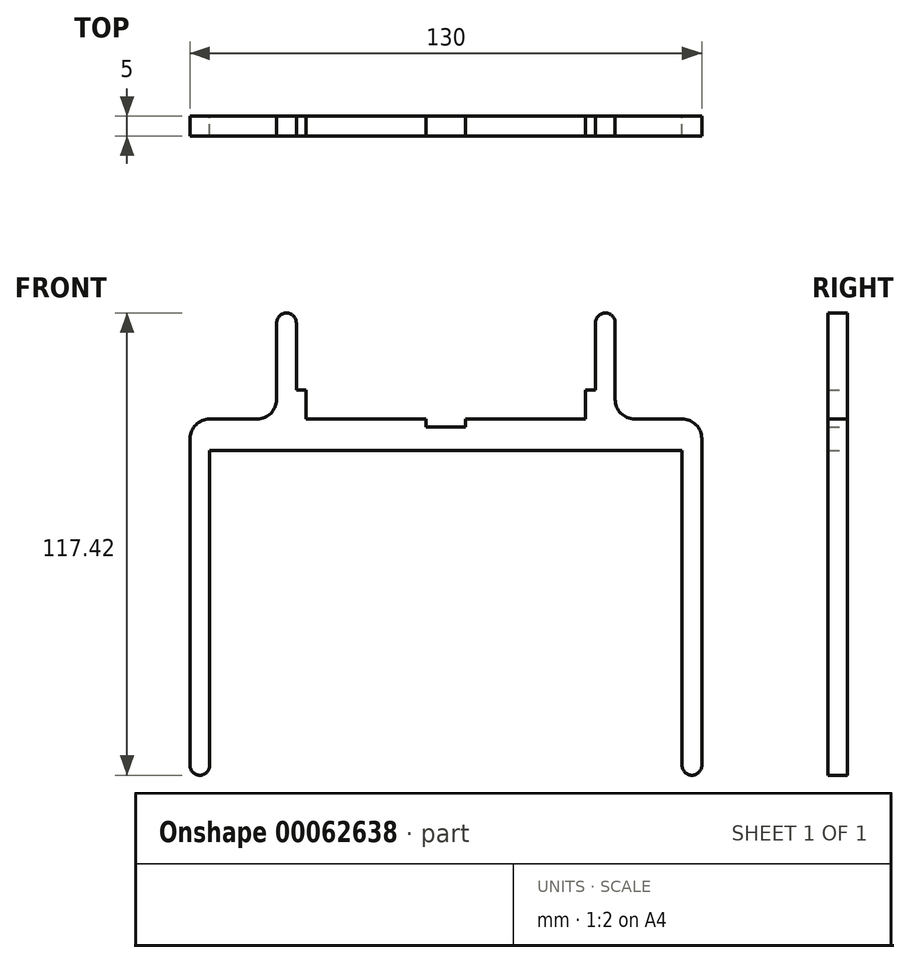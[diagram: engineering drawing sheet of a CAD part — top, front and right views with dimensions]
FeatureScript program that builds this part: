
annotation { "Feature Type Name" : "Feature", "Feature Type Description" : "" }
export const myFeature = defineFeature(function(context is Context, id is Id, definition is map)
    precondition{}
    {
        {
            var Q0;
            Q0=qCreatedBy(makeId("Front.planeOp"),FACE);
            var sketch = newSketch(context, id + "F0", { "sketchPlane" : qUnion([Q0])});
            skLineSegment(sketch, "E0.bottom", {"start": v(-60, 0) * mm, "end": v(0, 0) * mm});
            skLineSegment(sketch, "E0.top", {"start": v(-60, 8) * mm, "end": v(-43, 8) * mm});
            skLineSegment(sketch, "E1.bottom", {"start": v(-60, 8) * mm, "end": v(-65, 8) * mm});
            skLineSegment(sketch, "E1.left", {"start": v(-60, 0) * mm, "end": v(-60, -80) * mm});
            skLineSegment(sketch, "E1.right", {"start": v(-65, 8) * mm, "end": v(-65, -80) * mm});
            skPoint(sketch, "E2", {"position": v(-35.5, 8) * mm});
            skLineSegment(sketch, "E3.top", {"start": v(-35.5, 15.42) * mm, "end": v(-38, 15.42) * mm});
            skLineSegment(sketch, "E3.left", {"start": v(-35.5, 8) * mm, "end": v(-35.5, 15.42) * mm});
            skLineSegment(sketch, "E4.left", {"start": v(-38, 15.42) * mm, "end": v(-38, 32.42) * mm});
            skLineSegment(sketch, "E4.right", {"start": v(-43, 8) * mm, "end": v(-43, 32.42) * mm});
            skLineSegment(sketch, "E5.trimOffspring", {"start": v(-35.5, 8) * mm, "end": v(0, 8) * mm});
            skArc(sketch, "E6", {"start": v(-38, 32.42) * mm, "mid": v(-40.5, 34.92) * mm, "end": v(-43, 32.42) * mm});
            skArc(sketch, "E7", {"start": v(-65, -80) * mm, "mid": v(-62.5, -82.5) * mm, "end": v(-60, -80) * mm});
            skArc(sketch, "E8.MirrorCS", {"start": v(38, 32.42) * mm, "mid": v(40.5, 34.92) * mm, "end": v(43, 32.42) * mm});
            skLineSegment(sketch, "E9.MirrorCS", {"start": v(35.5, 15.42) * mm, "end": v(38, 15.42) * mm});
            skLineSegment(sketch, "E10.MirrorCS", {"start": v(60, 8) * mm, "end": v(65, 8) * mm});
            skLineSegment(sketch, "E11.MirrorCS", {"start": v(60, 8) * mm, "end": v(43, 8) * mm});
            skLineSegment(sketch, "E12.MirrorCS", {"start": v(35.5, 8) * mm, "end": v(35.5, 15.42) * mm});
            skLineSegment(sketch, "E13.MirrorCS", {"start": v(65, 8) * mm, "end": v(65, -80) * mm});
            skPoint(sketch, "E14.MirrorP", {"position": v(35.5, 8) * mm});
            skLineSegment(sketch, "E15.MirrorCS", {"start": v(60, 0) * mm, "end": v(60, -80) * mm});
            skLineSegment(sketch, "E16.MirrorCS", {"start": v(43, 8) * mm, "end": v(43, 32.42) * mm});
            skArc(sketch, "E17.MirrorCS", {"start": v(65, -80) * mm, "mid": v(62.5, -82.5) * mm, "end": v(60, -80) * mm});
            skLineSegment(sketch, "E18.MirrorCS", {"start": v(38, 15.42) * mm, "end": v(38, 32.42) * mm});
            skLineSegment(sketch, "E19.MirrorCS", {"start": v(35.5, 8) * mm, "end": v(0, 8) * mm});
            skLineSegment(sketch, "E20.MirrorCS", {"start": v(60, 0) * mm, "end": v(0, 0) * mm});
            skSolve(sketch);
        }
        {
            var Q0;
            Q0 = qSketchRegion(id + "F0", true);
            extrude(context, id + "F1", {"entities" : qUnion([Q0]), "depth" : 5 * mm});
        }
        {
            var Q0;
            Q0=qCreatedBy(makeId("Front.planeOp"),FACE);
            var sketch = newSketch(context, id + "F2", { "sketchPlane" : qUnion([Q0])});
            skLineSegment(sketch, "E21.rect.bottom", {"start": v(5, 6) * mm, "end": v(-5, 6) * mm});
            skLineSegment(sketch, "E21.rect.top", {"start": v(5, 10) * mm, "end": v(-5, 10) * mm});
            skLineSegment(sketch, "E21.rect.left", {"start": v(5, 6) * mm, "end": v(5, 10) * mm});
            skLineSegment(sketch, "E21.rect.right", {"start": v(-5, 6) * mm, "end": v(-5, 10) * mm});
            skPoint(sketch, "E21.rect.middle", {"position": v(0, 8) * mm});
            skSolve(sketch);
        }
        {
            var Q0;
            Q0 = qSketchRegion(id + "F2", true);
            extrude(context, id + "F3", {"entities" : qUnion([Q0]), "operationType" : NewBodyOperationType.REMOVE, "depth" : 25 * mm});
        }
        {
            var Q0;
            Q0=makeQuery(id+"F1.opExtrude","SWEPT_EDGE",EDGE,{"disambiguationData":[OSD([sQuery(id+"F0.wireOp",EDGE,"E1.bottom"),sQuery(id+"F0.wireOp",EDGE,"E1.right")])]});
            var Q1;
            Q1=makeQuery(id+"F1.opExtrude","SWEPT_EDGE",EDGE,{"disambiguationData":[OSD([sQuery(id+"F0.wireOp",EDGE,"E10.MirrorCS"),sQuery(id+"F0.wireOp",EDGE,"E13.MirrorCS")])]});
            fillet(context, id + "F4", {"entities" : qUnion([Q0, Q1]), "radius" : 5 * mm, "tangentPropagation" : true, "allowEdgeOverflow" : false});
        }
        {
            var Q0;
            Q0=makeQuery(id+"F1.opExtrude","SWEPT_EDGE",EDGE,{"disambiguationData":[OSD([sQuery(id+"F0.wireOp",EDGE,"E0.top"),sQuery(id+"F0.wireOp",EDGE,"E4.right")])]});
            var Q1;
            Q1=makeQuery(id+"F1.opExtrude","SWEPT_EDGE",EDGE,{"disambiguationData":[OSD([sQuery(id+"F0.wireOp",EDGE,"E11.MirrorCS"),sQuery(id+"F0.wireOp",EDGE,"E16.MirrorCS")])]});
            fillet(context, id + "F5", {"entities" : qUnion([Q0, Q1]), "radius" : 5 * mm, "tangentPropagation" : true, "allowEdgeOverflow" : false});
        }
    });
